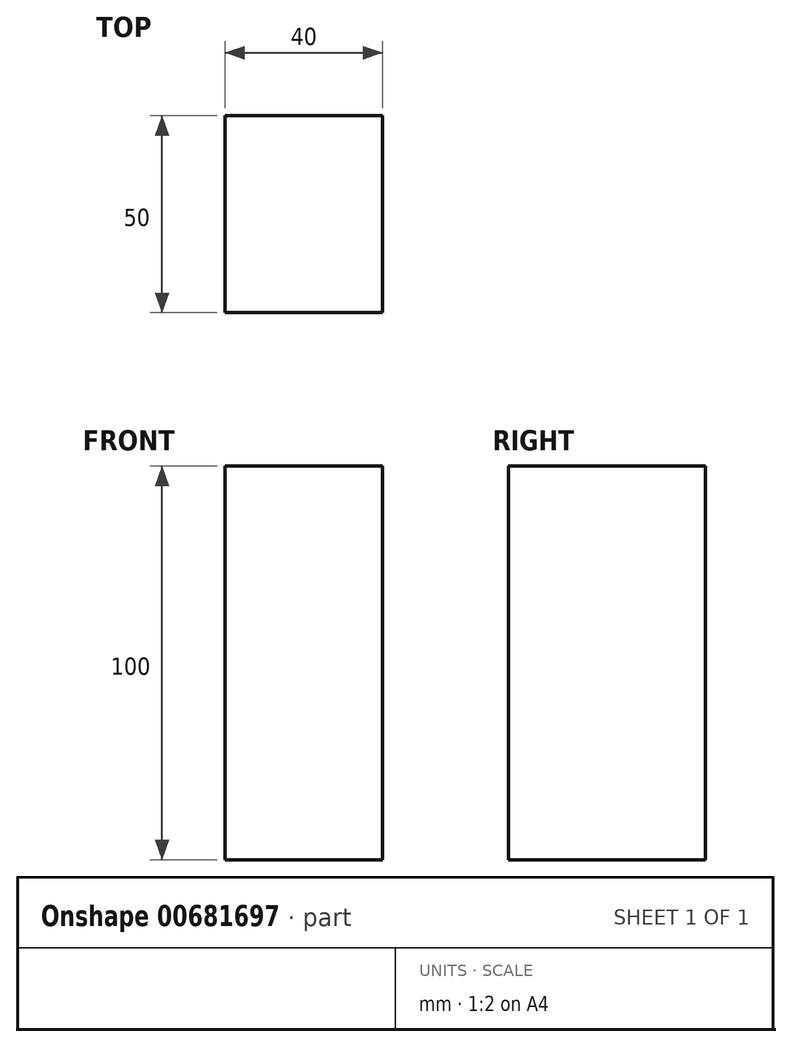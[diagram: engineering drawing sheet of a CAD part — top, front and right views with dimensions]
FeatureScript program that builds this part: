
annotation { "Feature Type Name" : "Feature", "Feature Type Description" : "" }
export const myFeature = defineFeature(function(context is Context, id is Id, definition is map)
    precondition{}
    {
        {
            var Q0;
            Q0=qCreatedBy(makeId("Front.planeOp"),FACE);
            var sketch = newSketch(context, id + "F0", { "sketchPlane" : qUnion([Q0])});
            skLineSegment(sketch, "E0.bottom", {"start": v(-53.67, 95.4) * mm, "end": v(-13.67, 95.4) * mm});
            skLineSegment(sketch, "E0.top", {"start": v(-53.67, -4.6) * mm, "end": v(-13.67, -4.6) * mm});
            skLineSegment(sketch, "E0.left", {"start": v(-53.67, 95.4) * mm, "end": v(-53.67, -4.6) * mm});
            skLineSegment(sketch, "E0.right", {"start": v(-13.67, 95.4) * mm, "end": v(-13.67, -4.6) * mm});
            skSolve(sketch);
        }
        {
            var Q0;
            Q0 = qSketchRegion(id + "F0", true);
            extrude(context, id + "F1", {"entities" : qUnion([Q0]), "depth" : 50 * mm, "offsetDistance" : 25.4 * mm});
        }
    });
